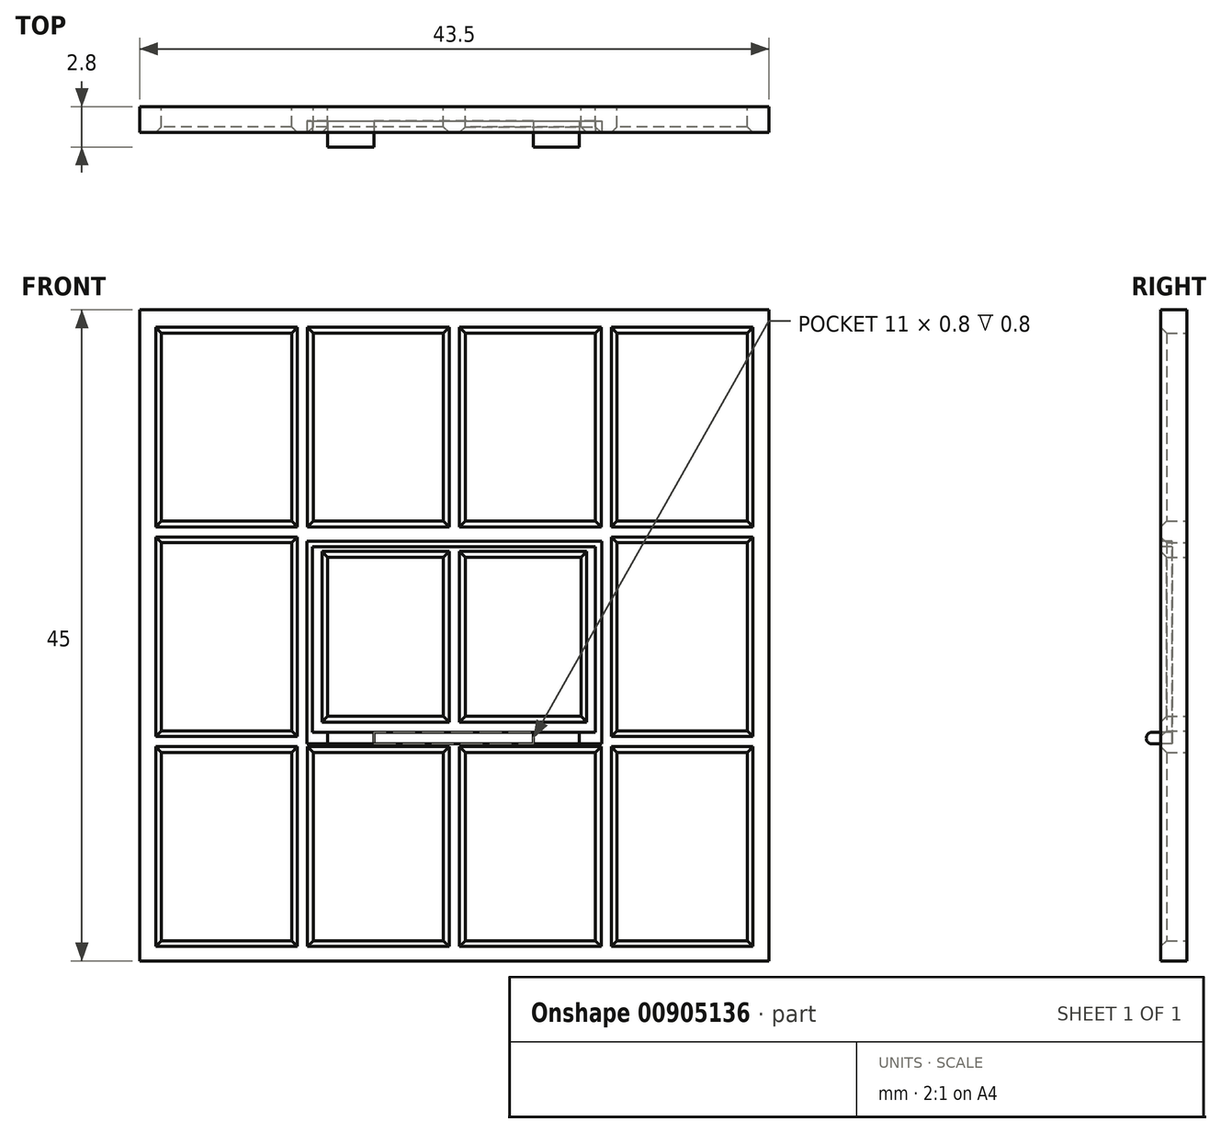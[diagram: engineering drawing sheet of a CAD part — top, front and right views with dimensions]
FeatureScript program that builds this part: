
annotation { "Feature Type Name" : "Feature", "Feature Type Description" : "" }
export const myFeature = defineFeature(function(context is Context, id is Id, definition is map)
    precondition{}
    {
        {
            var Q0;
            Q0=qCreatedBy(makeId("Front.planeOp"),FACE);
            var sketch = newSketch(context, id + "F0", { "sketchPlane" : qUnion([Q0])});
            skLineSegment(sketch, "E0.bottom", {"start": v(22, -22.5) * mm, "end": v(-22, -22.5) * mm});
            skLineSegment(sketch, "E0.top", {"start": v(22, 22.5) * mm, "end": v(-22, 22.5) * mm});
            skLineSegment(sketch, "E0.left", {"start": v(21.5, -22.5) * mm, "end": v(21.5, 22.5) * mm});
            skLineSegment(sketch, "E0.right", {"start": v(-22, -22.5) * mm, "end": v(-22, 22.5) * mm});
            skPoint(sketch, "E0.middle", {"position": v(-0.5, 0) * mm});
            skLineSegment(sketch, "E1", {"start": v(0, -22.5) * mm, "end": v(22, -22.5) * mm, "construction": true});
            skLineSegment(sketch, "E2", {"start": v(0, -22.5) * mm, "end": v(-22, -22.5) * mm, "construction": true});
            skLineSegment(sketch, "E3", {"start": v(-22, 22.5) * mm, "end": v(22, 22.5) * mm, "construction": true});
            skLineSegment(sketch, "E4", {"start": v(-22, 22.5) * mm, "end": v(-22, 7.5) * mm, "construction": true});
            skLineSegment(sketch, "E5", {"start": v(-22, 7.9) * mm, "end": v(22, 7.9) * mm, "construction": true});
            skLineSegment(sketch, "E6", {"start": v(-22, -22.5) * mm, "end": v(-22, -7.5) * mm});
            skLineSegment(sketch, "E7", {"start": v(-22, -7.1) * mm, "end": v(22, -7.1) * mm, "construction": true});
            skLineSegment(sketch, "E8", {"start": v(-22, -14.6) * mm, "end": v(-11, -14.6) * mm, "construction": true});
            skLineSegment(sketch, "E9", {"start": v(-16, -14.6) * mm, "end": v(-16, -7.1) * mm, "construction": true});
            skLineSegment(sketch, "E10.bottom", {"start": v(-20.5, -8.1) * mm, "end": v(-11.5, -8.1) * mm});
            skLineSegment(sketch, "E10.top", {"start": v(-20.5, -21.1) * mm, "end": v(-11.5, -21.1) * mm});
            skLineSegment(sketch, "E10.left", {"start": v(-20.5, -8.1) * mm, "end": v(-20.5, -21.1) * mm});
            skLineSegment(sketch, "E10.right", {"start": v(-11.5, -8.1) * mm, "end": v(-11.5, -21.1) * mm});
            skPoint(sketch, "E10.middle", {"position": v(-16, -14.6) * mm});
            skLineSegment(sketch, "E11.1.0.0", {"start": v(-10, -8.1) * mm, "end": v(-1, -8.1) * mm});
            skLineSegment(sketch, "E11.1.0.1", {"start": v(-1, -8.1) * mm, "end": v(-1, -21.1) * mm});
            skLineSegment(sketch, "E11.1.0.2", {"start": v(-10, -21.1) * mm, "end": v(-1, -21.1) * mm});
            skLineSegment(sketch, "E11.1.0.3", {"start": v(-10, -8.1) * mm, "end": v(-10, -21.1) * mm});
            skLineSegment(sketch, "E11.2.0.0", {"start": v(0.5, -8.1) * mm, "end": v(9.5, -8.1) * mm});
            skLineSegment(sketch, "E11.2.0.1", {"start": v(9.5, -8.1) * mm, "end": v(9.5, -21.1) * mm});
            skLineSegment(sketch, "E11.2.0.2", {"start": v(0.5, -21.1) * mm, "end": v(9.5, -21.1) * mm});
            skLineSegment(sketch, "E11.2.0.3", {"start": v(0.5, -8.1) * mm, "end": v(0.5, -21.1) * mm});
            skLineSegment(sketch, "E11.3.0.0", {"start": v(11, -8.1) * mm, "end": v(20, -8.1) * mm});
            skLineSegment(sketch, "E11.3.0.1", {"start": v(20, -8.1) * mm, "end": v(20, -21.1) * mm});
            skLineSegment(sketch, "E11.3.0.2", {"start": v(11, -21.1) * mm, "end": v(20, -21.1) * mm});
            skLineSegment(sketch, "E11.3.0.3", {"start": v(11, -8.1) * mm, "end": v(11, -21.1) * mm});
            skLineSegment(sketch, "E12.1.0.0", {"start": v(-20.5, 6.4) * mm, "end": v(-11.5, 6.4) * mm});
            skLineSegment(sketch, "E12.1.0.1", {"start": v(-11.5, 6.4) * mm, "end": v(-11.5, -6.6) * mm});
            skLineSegment(sketch, "E12.1.0.2", {"start": v(-20.5, -6.6) * mm, "end": v(-11.5, -6.6) * mm});
            skLineSegment(sketch, "E12.1.0.3", {"start": v(-20.5, 6.4) * mm, "end": v(-20.5, -6.6) * mm});
            skLineSegment(sketch, "E12.1.0.4", {"start": v(-10, 6.4) * mm, "end": v(-10, -6.6) * mm});
            skLineSegment(sketch, "E12.1.0.5", {"start": v(-10, 6.4) * mm, "end": v(-1, 6.4) * mm});
            skLineSegment(sketch, "E12.1.0.6", {"start": v(-1, 6.4) * mm, "end": v(-1, -6.6) * mm});
            skLineSegment(sketch, "E12.1.0.7", {"start": v(-10, -6.6) * mm, "end": v(-1, -6.6) * mm});
            skLineSegment(sketch, "E12.1.0.8", {"start": v(0.5, -6.6) * mm, "end": v(9.5, -6.6) * mm});
            skLineSegment(sketch, "E12.1.0.9", {"start": v(0.5, 6.4) * mm, "end": v(0.5, -6.6) * mm});
            skLineSegment(sketch, "E12.1.0.10", {"start": v(0.5, 6.4) * mm, "end": v(9.5, 6.4) * mm});
            skLineSegment(sketch, "E12.1.0.11", {"start": v(9.5, 6.4) * mm, "end": v(9.5, -6.6) * mm});
            skLineSegment(sketch, "E12.1.0.12", {"start": v(11, 6.4) * mm, "end": v(11, -6.6) * mm});
            skLineSegment(sketch, "E12.1.0.13", {"start": v(11, 6.4) * mm, "end": v(20, 6.4) * mm});
            skLineSegment(sketch, "E12.1.0.14", {"start": v(20, 6.4) * mm, "end": v(20, -6.6) * mm});
            skLineSegment(sketch, "E12.1.0.15", {"start": v(11, -6.6) * mm, "end": v(20, -6.6) * mm});
            skLineSegment(sketch, "E12.2.0.0", {"start": v(-20.5, 20.9) * mm, "end": v(-11.5, 20.9) * mm});
            skLineSegment(sketch, "E12.2.0.1", {"start": v(-11.5, 20.9) * mm, "end": v(-11.5, 7.9) * mm});
            skLineSegment(sketch, "E12.2.0.2", {"start": v(-20.5, 7.9) * mm, "end": v(-11.5, 7.9) * mm});
            skLineSegment(sketch, "E12.2.0.3", {"start": v(-20.5, 20.9) * mm, "end": v(-20.5, 7.9) * mm});
            skLineSegment(sketch, "E12.2.0.4", {"start": v(-10, 20.9) * mm, "end": v(-10, 7.9) * mm});
            skLineSegment(sketch, "E12.2.0.5", {"start": v(-10, 20.9) * mm, "end": v(-1, 20.9) * mm});
            skLineSegment(sketch, "E12.2.0.6", {"start": v(-1, 20.9) * mm, "end": v(-1, 7.9) * mm});
            skLineSegment(sketch, "E12.2.0.7", {"start": v(-10, 7.9) * mm, "end": v(-1, 7.9) * mm});
            skLineSegment(sketch, "E12.2.0.8", {"start": v(0.5, 7.9) * mm, "end": v(9.5, 7.9) * mm});
            skLineSegment(sketch, "E12.2.0.9", {"start": v(0.5, 20.9) * mm, "end": v(0.5, 7.9) * mm});
            skLineSegment(sketch, "E12.2.0.10", {"start": v(0.5, 20.9) * mm, "end": v(9.5, 20.9) * mm});
            skLineSegment(sketch, "E12.2.0.11", {"start": v(9.5, 20.9) * mm, "end": v(9.5, 7.9) * mm});
            skLineSegment(sketch, "E12.2.0.12", {"start": v(11, 20.9) * mm, "end": v(11, 7.9) * mm});
            skLineSegment(sketch, "E12.2.0.13", {"start": v(11, 20.9) * mm, "end": v(20, 20.9) * mm});
            skLineSegment(sketch, "E12.2.0.14", {"start": v(20, 20.9) * mm, "end": v(20, 7.9) * mm});
            skLineSegment(sketch, "E12.2.0.15", {"start": v(11, 7.9) * mm, "end": v(20, 7.9) * mm});
            skLineSegment(sketch, "E12.direction1", {"start": v(-20.5, -21.1) * mm, "end": v(-20.5, -6.2) * mm, "construction": true});
            skLineSegment(sketch, "E13", {"start": v(-22, -22.5) * mm, "end": v(-24, -22.5) * mm});
            skLineSegment(sketch, "E14", {"start": v(-24, -22.5) * mm, "end": v(-24, -24.5) * mm});
            skLineSegment(sketch, "E15", {"start": v(24, -24.5) * mm, "end": v(24, -22.5) * mm});
            skLineSegment(sketch, "E16", {"start": v(22, -22.5) * mm, "end": v(24, -22.5) * mm});
            skLineSegment(sketch, "E17", {"start": v(-12, -8.1) * mm, "end": v(-10.5, -8.1) * mm, "construction": true});
            skLineSegment(sketch, "E18", {"start": v(-1, -8.1) * mm, "end": v(1, -8.1) * mm, "construction": true});
            skLineSegment(sketch, "E19", {"start": v(-10, -6.2) * mm, "end": v(-10, -8.1) * mm, "construction": true});
            skLineSegment(sketch, "E20", {"start": v(11, 7.9) * mm, "end": v(11, 6.4) * mm, "construction": true});
            skLineSegment(sketch, "E21", {"start": v(11, 20.9) * mm, "end": v(9.5, 20.9) * mm, "construction": true});
            skSolve(sketch);
        }
        {
            var Q0;
            {var subQ4=sQuery(id+"F0.wireOp",EDGE,"E0.left");Q0=makeQuery(id+"F0.imprint","IMPRINT",FACE,{"disambiguationData":[TD([[makeQuery(id+"F0.imprint","IMPRINT",EDGE,{"derivedFrom":subQ4}),1.0]])]});}
            extrude(context, id + "F1", {"entities" : qUnion([Q0]), "depth" : 1.8 * mm, "offsetDistance" : 25 * mm});
        }
        {
            var Q0;
            Q0=makeQuery(id+"F1.opExtrude","SWEPT_FACE",FACE,{"disambiguationData":[OSD([sQuery(id+"F0.wireOp",EDGE,"E12.1.0.11")])]});
            extrude(context, id + "F2", {"entities" : qUnion([Q0]), "operationType" : NewBodyOperationType.ADD, "depth" : 1 * mm, "offsetDistance" : 25 * mm});
        }
        {
            var Q0;
            Q0=makeQuery(id+"F1.opExtrude","SWEPT_FACE",FACE,{"disambiguationData":[OSD([sQuery(id+"F0.wireOp",EDGE,"E12.1.0.4")])]});
            extrude(context, id + "F3", {"entities" : qUnion([Q0]), "operationType" : NewBodyOperationType.ADD, "depth" : 1 * mm, "offsetDistance" : 25 * mm});
        }
        {
            var Q0;
            Q0=makeQuery(id+"F1.opExtrude","SWEPT_FACE",FACE,{"disambiguationData":[OSD([sQuery(id+"F0.wireOp",EDGE,"E12.1.0.5")])]});
            var Q1;
            Q1=makeQuery(id+"F1.opExtrude","SWEPT_FACE",FACE,{"disambiguationData":[OSD([sQuery(id+"F0.wireOp",EDGE,"E12.1.0.10")])]});
            extrude(context, id + "F4", {"entities" : qUnion([Q0, Q1]), "operationType" : NewBodyOperationType.ADD, "depth" : 1 * mm, "offsetDistance" : 25 * mm});
        }
        {
            var Q0;
            Q0=makeQuery(id+"F1.opExtrude","SWEPT_FACE",FACE,{"disambiguationData":[OSD([sQuery(id+"F0.wireOp",EDGE,"E12.1.0.7")])]});
            var Q1;
            Q1=makeQuery(id+"F1.opExtrude","SWEPT_FACE",FACE,{"disambiguationData":[OSD([sQuery(id+"F0.wireOp",EDGE,"E12.1.0.8")])]});
            extrude(context, id + "F5", {"entities" : qUnion([Q0, Q1]), "operationType" : NewBodyOperationType.ADD, "depth" : 1 * mm, "offsetDistance" : 25 * mm});
        }
        {
            var Q0;
            {var subQ0=sQuery(id+"F0.wireOp",EDGE,"E12.1.0.7");var subQ1=sQuery(id+"F0.wireOp",EDGE,"E12.1.0.8");var subQ2=sQuery(id+"F0.wireOp",EDGE,"E12.1.0.5");var subQ3=sQuery(id+"F0.wireOp",EDGE,"E12.1.0.10");var subQ4=sQuery(id+"F0.wireOp",EDGE,"E12.1.0.4");var subQ5=sQuery(id+"F0.wireOp",EDGE,"E12.1.0.11");Q0=makeQuery(id+"F5.boolean.opBoolean","MERGE",FACE,{"derivedFrom":[makeQuery(id+"F4.boolean.opBoolean","MERGE",FACE,{"derivedFrom":[makeQuery(id+"F3.boolean.opBoolean","MERGE",FACE,{"derivedFrom":[makeQuery(id+"F2.boolean.opBoolean","MERGE",FACE,{"derivedFrom":[makeQuery(id+"F1.opExtrude","CAP_FACE",FACE,{"disambiguationData":[OSD([sQuery(id+"F0.wireOp",EDGE,"E0.bottom"),sQuery(id+"F0.wireOp",EDGE,"E0.top"),sQuery(id+"F0.wireOp",EDGE,"E0.left"),sQuery(id+"F0.wireOp",EDGE,"E0.right"),sQuery(id+"F0.wireOp",EDGE,"E10.bottom"),sQuery(id+"F0.wireOp",EDGE,"E10.top"),sQuery(id+"F0.wireOp",EDGE,"E10.left"),sQuery(id+"F0.wireOp",EDGE,"E10.right"),sQuery(id+"F0.wireOp",EDGE,"E11.1.0.0"),sQuery(id+"F0.wireOp",EDGE,"E11.1.0.1"),sQuery(id+"F0.wireOp",EDGE,"E11.1.0.2"),sQuery(id+"F0.wireOp",EDGE,"E11.1.0.3"),sQuery(id+"F0.wireOp",EDGE,"E11.2.0.0"),sQuery(id+"F0.wireOp",EDGE,"E11.2.0.1"),sQuery(id+"F0.wireOp",EDGE,"E11.2.0.2"),sQuery(id+"F0.wireOp",EDGE,"E11.2.0.3"),sQuery(id+"F0.wireOp",EDGE,"E11.3.0.0"),sQuery(id+"F0.wireOp",EDGE,"E11.3.0.1"),sQuery(id+"F0.wireOp",EDGE,"E11.3.0.2"),sQuery(id+"F0.wireOp",EDGE,"E11.3.0.3"),sQuery(id+"F0.wireOp",EDGE,"E12.1.0.0"),sQuery(id+"F0.wireOp",EDGE,"E12.1.0.1"),sQuery(id+"F0.wireOp",EDGE,"E12.1.0.2"),sQuery(id+"F0.wireOp",EDGE,"E12.1.0.3"),subQ4,subQ2,sQuery(id+"F0.wireOp",EDGE,"E12.1.0.6"),subQ0,subQ1,sQuery(id+"F0.wireOp",EDGE,"E12.1.0.9"),subQ3,subQ5,sQuery(id+"F0.wireOp",EDGE,"E12.1.0.12"),sQuery(id+"F0.wireOp",EDGE,"E12.1.0.13"),sQuery(id+"F0.wireOp",EDGE,"E12.1.0.14"),sQuery(id+"F0.wireOp",EDGE,"E12.1.0.15"),sQuery(id+"F0.wireOp",EDGE,"E12.2.0.0"),sQuery(id+"F0.wireOp",EDGE,"E12.2.0.1"),sQuery(id+"F0.wireOp",EDGE,"E12.2.0.2"),sQuery(id+"F0.wireOp",EDGE,"E12.2.0.3"),sQuery(id+"F0.wireOp",EDGE,"E12.2.0.4"),sQuery(id+"F0.wireOp",EDGE,"E12.2.0.5"),sQuery(id+"F0.wireOp",EDGE,"E12.2.0.6"),sQuery(id+"F0.wireOp",EDGE,"E12.2.0.7"),sQuery(id+"F0.wireOp",EDGE,"E12.2.0.8"),sQuery(id+"F0.wireOp",EDGE,"E12.2.0.9"),sQuery(id+"F0.wireOp",EDGE,"E12.2.0.10"),sQuery(id+"F0.wireOp",EDGE,"E12.2.0.11"),sQuery(id+"F0.wireOp",EDGE,"E12.2.0.12"),sQuery(id+"F0.wireOp",EDGE,"E12.2.0.13"),sQuery(id+"F0.wireOp",EDGE,"E12.2.0.14"),sQuery(id+"F0.wireOp",EDGE,"E12.2.0.15")])],"isStart":false}),makeQuery(id+"F2.opExtrude","SWEPT_FACE",FACE,{"disambiguationData":[OSD([subQ5]),TDD([makeQuery(id+"F1.opExtrude","CAP_EDGE",EDGE,{"disambiguationData":[OSD([subQ5])],"isStart":false})])]})]}),makeQuery(id+"F3.opExtrude","SWEPT_FACE",FACE,{"disambiguationData":[OSD([subQ4]),TDD([makeQuery(id+"F1.opExtrude","CAP_EDGE",EDGE,{"disambiguationData":[OSD([subQ4])],"isStart":false})])]})]}),makeQuery(id+"F4.opExtrude","SWEPT_FACE",FACE,{"disambiguationData":[OSD([subQ3]),TDD([makeQuery(id+"F1.opExtrude","CAP_EDGE",EDGE,{"disambiguationData":[OSD([subQ3])],"isStart":false})])]}),makeQuery(id+"F4.opExtrude","SWEPT_FACE",FACE,{"disambiguationData":[OSD([subQ2]),TDD([makeQuery(id+"F1.opExtrude","CAP_EDGE",EDGE,{"disambiguationData":[OSD([subQ2])],"isStart":false})])]})]}),makeQuery(id+"F5.opExtrude","SWEPT_FACE",FACE,{"disambiguationData":[OSD([subQ1]),TDD([makeQuery(id+"F1.opExtrude","CAP_EDGE",EDGE,{"disambiguationData":[OSD([subQ1])],"isStart":false})])]}),makeQuery(id+"F5.opExtrude","SWEPT_FACE",FACE,{"disambiguationData":[OSD([subQ0]),TDD([makeQuery(id+"F1.opExtrude","CAP_EDGE",EDGE,{"disambiguationData":[OSD([subQ0])],"isStart":false})])]})]});}
            var sketch = newSketch(context, id + "F6", { "sketchPlane" : qUnion([Q0])});
            skPoint(sketch, "E22.middle", {"position": v(-0.3, 0) * mm});
            skLineSegment(sketch, "E23.bottom", {"start": v(9.9, -6.7) * mm, "end": v(-10.5, -6.7) * mm});
            skLineSegment(sketch, "E24", {"start": v(-10.5, -6.7) * mm, "end": v(-9, -6.7) * mm, "construction": true});
            skLineSegment(sketch, "E25", {"start": v(-9, -6.7) * mm, "end": v(-9, -7.5) * mm, "construction": true});
            skLineSegment(sketch, "E26", {"start": v(-9, -6.7) * mm, "end": v(-9, -7.5) * mm});
            skLineSegment(sketch, "E27", {"start": v(-9, -7.5) * mm, "end": v(-5.8, -7.5) * mm});
            skLineSegment(sketch, "E28", {"start": v(-5.8, -6.7) * mm, "end": v(-5.8, -7.5) * mm});
            skLineSegment(sketch, "E29", {"start": v(9.9, -6.7) * mm, "end": v(8.4, -6.7) * mm});
            skLineSegment(sketch, "E30", {"start": v(8.4, -7.5) * mm, "end": v(8.4, -6.7) * mm});
            skLineSegment(sketch, "E31", {"start": v(8.4, -7.5) * mm, "end": v(5.2, -7.5) * mm});
            skLineSegment(sketch, "E32", {"start": v(5.2, -6.7) * mm, "end": v(5.2, -7.5) * mm});
            skLineSegment(sketch, "E33", {"start": v(-1, -5.6) * mm, "end": v(0.5, -5.6) * mm, "construction": true});
            skLineSegment(sketch, "E34", {"start": v(0.5, -5.6) * mm, "end": v(-0.25, -5.6) * mm, "construction": true});
            skLineSegment(sketch, "E35", {"start": v(-0.25, -7.5) * mm, "end": v(-0.25, -5.6) * mm, "construction": true});
            skLineSegment(sketch, "E36", {"start": v(-0.25, -7.5) * mm, "end": v(9.95, -7.5) * mm});
            skLineSegment(sketch, "E37", {"start": v(-0.25, -7.5) * mm, "end": v(-10.45, -7.5) * mm});
            skLineSegment(sketch, "E38.bottom", {"start": v(-10.45, -7.5) * mm, "end": v(9.95, -7.5) * mm});
            skLineSegment(sketch, "E38.top", {"start": v(-10.45, 6.52) * mm, "end": v(9.95, 6.52) * mm});
            skLineSegment(sketch, "E38.left", {"start": v(-10.45, -7.5) * mm, "end": v(-10.45, 6.52) * mm});
            skLineSegment(sketch, "E38.right", {"start": v(9.95, -7.5) * mm, "end": v(9.95, 6.52) * mm});
            skLineSegment(sketch, "E39", {"start": v(-10.45, 6.52) * mm, "end": v(-10.45, 6.12) * mm, "construction": true});
            skLineSegment(sketch, "E40", {"start": v(-10.45, 6.12) * mm, "end": v(-10.05, 6.12) * mm, "construction": true});
            skLineSegment(sketch, "E41", {"start": v(9.9, -6.7) * mm, "end": v(9.5, -6.7) * mm, "construction": true});
            skLineSegment(sketch, "E42", {"start": v(9.5, -6.7) * mm, "end": v(9.5, -7.5) * mm, "construction": true});
            skLineSegment(sketch, "E43.bottom", {"start": v(-10.05, 6.12) * mm, "end": v(9.5, 6.12) * mm});
            skLineSegment(sketch, "E43.top", {"start": v(-10.05, -6.7) * mm, "end": v(9.5, -6.7) * mm});
            skLineSegment(sketch, "E43.left", {"start": v(-10.05, 6.12) * mm, "end": v(-10.05, -6.7) * mm});
            skLineSegment(sketch, "E43.right", {"start": v(9.5, 6.12) * mm, "end": v(9.5, -6.7) * mm});
            skLineSegment(sketch, "E44.bottom", {"start": v(-9, -6.7) * mm, "end": v(-5.8, -6.7) * mm});
            skSolve(sketch);
        }
        {
            var Q0;
            Q0=makeQuery(id+"F6.imprint","IMPRINT",FACE,{"disambiguationData":[TD([[makeQuery(id+"F6.imprint","IMPRINT",EDGE,{"derivedFrom":sQuery(id+"F6.wireOp",EDGE,"E22.bottom")}),-1.0]])]});
            var Q1;
            {var subQ0=sQuery(id+"F6.wireOp",EDGE,"E28");Q1=makeQuery(id+"F6.imprint","IMPRINT",FACE,{"disambiguationData":[TD([[makeQuery(id+"F6.imprint","IMPRINT",EDGE,{"derivedFrom":subQ0}),1.0]])]});}
            var Q2;
            {var subQ7=sQuery(id+"F6.wireOp",EDGE,"E26");Q2=makeQuery(id+"F6.imprint","IMPRINT",FACE,{"disambiguationData":[TD([[makeQuery(id+"F6.imprint","IMPRINT",EDGE,{"derivedFrom":subQ7}),-1.0]])]});}
            var Q3;
            {var subQ1=sQuery(id+"F6.wireOp",EDGE,"E30");Q3=makeQuery(id+"F6.imprint","IMPRINT",FACE,{"disambiguationData":[TD([[makeQuery(id+"F6.imprint","IMPRINT",EDGE,{"derivedFrom":subQ1}),-1.0]])]});}
            var Q4;
            {var subQ0=sQuery(id+"F6.wireOp",EDGE,"E32");Q4=makeQuery(id+"F6.imprint","IMPRINT",FACE,{"disambiguationData":[TD([[makeQuery(id+"F6.imprint","IMPRINT",EDGE,{"derivedFrom":subQ0}),-1.0]])]});}
            var Q5;
            {var subQ3=sQuery(id+"F6.wireOp",EDGE,"E26");Q5=makeQuery(id+"F6.imprint","IMPRINT",FACE,{"disambiguationData":[TD([[makeQuery(id+"F6.imprint","IMPRINT",EDGE,{"derivedFrom":subQ3}),-1.0]])]});}
            extrude(context, id + "F7", {"entities" : qUnion([Q0, Q1, Q2, Q3, Q4, Q5]), "operationType" : NewBodyOperationType.REMOVE, "oppositeDirection" : true, "depth" : .8 * mm, "offsetDistance" : 25 * mm});
        }
        {
            var Q0;
            {var subQ0=sQuery(id+"F0.wireOp",EDGE,"E12.1.0.7");var subQ1=sQuery(id+"F0.wireOp",EDGE,"E12.1.0.8");var subQ2=sQuery(id+"F0.wireOp",EDGE,"E12.1.0.5");var subQ3=sQuery(id+"F0.wireOp",EDGE,"E12.1.0.10");var subQ4=sQuery(id+"F0.wireOp",EDGE,"E12.1.0.4");var subQ5=sQuery(id+"F0.wireOp",EDGE,"E12.1.0.11");Q0=makeQuery(id+"F5.boolean.opBoolean","MERGE",FACE,{"derivedFrom":[makeQuery(id+"F4.boolean.opBoolean","MERGE",FACE,{"derivedFrom":[makeQuery(id+"F3.boolean.opBoolean","MERGE",FACE,{"derivedFrom":[makeQuery(id+"F2.boolean.opBoolean","MERGE",FACE,{"derivedFrom":[makeQuery(id+"F1.opExtrude","CAP_FACE",FACE,{"disambiguationData":[OSD([sQuery(id+"F0.wireOp",EDGE,"E0.bottom"),sQuery(id+"F0.wireOp",EDGE,"E0.top"),sQuery(id+"F0.wireOp",EDGE,"E0.left"),sQuery(id+"F0.wireOp",EDGE,"E0.right"),sQuery(id+"F0.wireOp",EDGE,"E10.bottom"),sQuery(id+"F0.wireOp",EDGE,"E10.top"),sQuery(id+"F0.wireOp",EDGE,"E10.left"),sQuery(id+"F0.wireOp",EDGE,"E10.right"),sQuery(id+"F0.wireOp",EDGE,"E11.1.0.0"),sQuery(id+"F0.wireOp",EDGE,"E11.1.0.1"),sQuery(id+"F0.wireOp",EDGE,"E11.1.0.2"),sQuery(id+"F0.wireOp",EDGE,"E11.1.0.3"),sQuery(id+"F0.wireOp",EDGE,"E11.2.0.0"),sQuery(id+"F0.wireOp",EDGE,"E11.2.0.1"),sQuery(id+"F0.wireOp",EDGE,"E11.2.0.2"),sQuery(id+"F0.wireOp",EDGE,"E11.2.0.3"),sQuery(id+"F0.wireOp",EDGE,"E11.3.0.0"),sQuery(id+"F0.wireOp",EDGE,"E11.3.0.1"),sQuery(id+"F0.wireOp",EDGE,"E11.3.0.2"),sQuery(id+"F0.wireOp",EDGE,"E11.3.0.3"),sQuery(id+"F0.wireOp",EDGE,"E12.1.0.0"),sQuery(id+"F0.wireOp",EDGE,"E12.1.0.1"),sQuery(id+"F0.wireOp",EDGE,"E12.1.0.2"),sQuery(id+"F0.wireOp",EDGE,"E12.1.0.3"),subQ4,subQ2,sQuery(id+"F0.wireOp",EDGE,"E12.1.0.6"),subQ0,subQ1,sQuery(id+"F0.wireOp",EDGE,"E12.1.0.9"),subQ3,subQ5,sQuery(id+"F0.wireOp",EDGE,"E12.1.0.12"),sQuery(id+"F0.wireOp",EDGE,"E12.1.0.13"),sQuery(id+"F0.wireOp",EDGE,"E12.1.0.14"),sQuery(id+"F0.wireOp",EDGE,"E12.1.0.15"),sQuery(id+"F0.wireOp",EDGE,"E12.2.0.0"),sQuery(id+"F0.wireOp",EDGE,"E12.2.0.1"),sQuery(id+"F0.wireOp",EDGE,"E12.2.0.2"),sQuery(id+"F0.wireOp",EDGE,"E12.2.0.3"),sQuery(id+"F0.wireOp",EDGE,"E12.2.0.4"),sQuery(id+"F0.wireOp",EDGE,"E12.2.0.5"),sQuery(id+"F0.wireOp",EDGE,"E12.2.0.6"),sQuery(id+"F0.wireOp",EDGE,"E12.2.0.7"),sQuery(id+"F0.wireOp",EDGE,"E12.2.0.8"),sQuery(id+"F0.wireOp",EDGE,"E12.2.0.9"),sQuery(id+"F0.wireOp",EDGE,"E12.2.0.10"),sQuery(id+"F0.wireOp",EDGE,"E12.2.0.11"),sQuery(id+"F0.wireOp",EDGE,"E12.2.0.12"),sQuery(id+"F0.wireOp",EDGE,"E12.2.0.13"),sQuery(id+"F0.wireOp",EDGE,"E12.2.0.14"),sQuery(id+"F0.wireOp",EDGE,"E12.2.0.15")])],"isStart":false}),makeQuery(id+"F2.opExtrude","SWEPT_FACE",FACE,{"disambiguationData":[OSD([subQ5]),TDD([makeQuery(id+"F1.opExtrude","CAP_EDGE",EDGE,{"disambiguationData":[OSD([subQ5])],"isStart":false})])]})]}),makeQuery(id+"F3.opExtrude","SWEPT_FACE",FACE,{"disambiguationData":[OSD([subQ4]),TDD([makeQuery(id+"F1.opExtrude","CAP_EDGE",EDGE,{"disambiguationData":[OSD([subQ4])],"isStart":false})])]})]}),makeQuery(id+"F4.opExtrude","SWEPT_FACE",FACE,{"disambiguationData":[OSD([subQ3]),TDD([makeQuery(id+"F1.opExtrude","CAP_EDGE",EDGE,{"disambiguationData":[OSD([subQ3])],"isStart":false})])]}),makeQuery(id+"F4.opExtrude","SWEPT_FACE",FACE,{"disambiguationData":[OSD([subQ2]),TDD([makeQuery(id+"F1.opExtrude","CAP_EDGE",EDGE,{"disambiguationData":[OSD([subQ2])],"isStart":false})])]})]}),makeQuery(id+"F5.opExtrude","SWEPT_FACE",FACE,{"disambiguationData":[OSD([subQ1]),TDD([makeQuery(id+"F1.opExtrude","CAP_EDGE",EDGE,{"disambiguationData":[OSD([subQ1])],"isStart":false})])]}),makeQuery(id+"F5.opExtrude","SWEPT_FACE",FACE,{"disambiguationData":[OSD([subQ0]),TDD([makeQuery(id+"F1.opExtrude","CAP_EDGE",EDGE,{"disambiguationData":[OSD([subQ0])],"isStart":false})])]})]});}
            var sketch = newSketch(context, id + "F8", { "sketchPlane" : qUnion([Q0])});
            skLineSegment(sketch, "E45.left", {"start": v(-10.45, -7.5) * mm, "end": v(-10.45, -8.3) * mm});
            skLineSegment(sketch, "E46.bottom", {"start": v(5.2, -6.7) * mm, "end": v(8.4, -6.7) * mm});
            skLineSegment(sketch, "E46.top", {"start": v(5.2, -7.5) * mm, "end": v(8.4, -7.5) * mm});
            skLineSegment(sketch, "E46.left", {"start": v(5.2, -6.7) * mm, "end": v(5.2, -7.5) * mm});
            skLineSegment(sketch, "E46.right", {"start": v(8.4, -6.7) * mm, "end": v(8.4, -7.5) * mm});
            skLineSegment(sketch, "E47.bottom", {"start": v(-9, -6.7) * mm, "end": v(-5.8, -6.7) * mm});
            skLineSegment(sketch, "E47.top", {"start": v(-9, -7.5) * mm, "end": v(-5.8, -7.5) * mm});
            skLineSegment(sketch, "E47.left", {"start": v(-9, -6.7) * mm, "end": v(-9, -7.5) * mm});
            skLineSegment(sketch, "E47.right", {"start": v(-5.8, -6.7) * mm, "end": v(-5.8, -7.5) * mm});
            skSolve(sketch);
        }
        {
            var Q0;
            Q0=makeQuery(id+"F8.imprint","IMPRINT",FACE,{"disambiguationData":[TD([[makeQuery(id+"F8.imprint","IMPRINT",EDGE,{"derivedFrom":sQuery(id+"F8.wireOp",EDGE,"E46.bottom")}),-1.0]])]});
            var Q1;
            Q1=makeQuery(id+"F8.imprint","IMPRINT",FACE,{"disambiguationData":[TD([[makeQuery(id+"F8.imprint","IMPRINT",EDGE,{"derivedFrom":sQuery(id+"F8.wireOp",EDGE,"E45.bottom")}),1.0]])]});
            var Q2;
            Q2=makeQuery(id+"F8.imprint","IMPRINT",FACE,{"disambiguationData":[TD([[makeQuery(id+"F8.imprint","IMPRINT",EDGE,{"derivedFrom":sQuery(id+"F8.wireOp",EDGE,"E47.bottom")}),-1.0]])]});
            extrude(context, id + "F9", {"entities" : qUnion([Q0, Q1, Q2]), "operationType" : NewBodyOperationType.ADD, "depth" : 1 * mm, "offsetDistance" : 25 * mm});
        }
        {
            var Q0;
            Q0=makeQuery(id+"F9.opExtrude","CAP_EDGE",EDGE,{"disambiguationData":[OSD([sQuery(id+"F8.wireOp",EDGE,"E45.bottom")])],"isStart":false});
            var Q1;
            Q1=makeQuery(id+"F9.opExtrude","CAP_EDGE",EDGE,{"disambiguationData":[OSD([sQuery(id+"F8.wireOp",EDGE,"E45.top")])],"isStart":false});
            var Q2;
            Q2=makeQuery(id+"F9.opExtrude","CAP_EDGE",EDGE,{"disambiguationData":[OSD([sQuery(id+"F8.wireOp",EDGE,"E46.bottom")])],"isStart":false});
            var Q3;
            Q3=makeQuery(id+"F9.opExtrude","CAP_EDGE",EDGE,{"disambiguationData":[OSD([sQuery(id+"F8.wireOp",EDGE,"E46.top")])],"isStart":false});
            var Q4;
            Q4=makeQuery(id+"F9.opExtrude","CAP_EDGE",EDGE,{"disambiguationData":[OSD([sQuery(id+"F8.wireOp",EDGE,"E47.top")])],"isStart":false});
            var Q5;
            Q5=makeQuery(id+"F9.opExtrude","CAP_EDGE",EDGE,{"disambiguationData":[OSD([sQuery(id+"F8.wireOp",EDGE,"E47.bottom")])],"isStart":false});
            fillet(context, id + "F10", {"entities" : qUnion([Q0, Q1, Q2, Q3, Q4, Q5]), "radius" : .4 * mm, "tangentPropagation" : true, "allowEdgeOverflow" : false});
        }
        {
            var Q0;
            Q0=makeQuery(id+"F1.opExtrude","CAP_EDGE",EDGE,{"disambiguationData":[OSD([sQuery(id+"F0.wireOp",EDGE,"E12.2.0.3")])],"isStart":false});
            var Q1;
            Q1=makeQuery(id+"F1.opExtrude","CAP_EDGE",EDGE,{"disambiguationData":[OSD([sQuery(id+"F0.wireOp",EDGE,"E12.2.0.1")])],"isStart":false});
            var Q2;
            Q2=makeQuery(id+"F1.opExtrude","CAP_EDGE",EDGE,{"disambiguationData":[OSD([sQuery(id+"F0.wireOp",EDGE,"E12.2.0.0")])],"isStart":false});
            var Q3;
            Q3=makeQuery(id+"F1.opExtrude","CAP_EDGE",EDGE,{"disambiguationData":[OSD([sQuery(id+"F0.wireOp",EDGE,"E12.2.0.2")])],"isStart":false});
            var Q4;
            Q4=makeQuery(id+"F1.opExtrude","CAP_EDGE",EDGE,{"disambiguationData":[OSD([sQuery(id+"F0.wireOp",EDGE,"E12.1.0.0")])],"isStart":false});
            var Q5;
            Q5=makeQuery(id+"F1.opExtrude","CAP_EDGE",EDGE,{"disambiguationData":[OSD([sQuery(id+"F0.wireOp",EDGE,"E12.1.0.3")])],"isStart":false});
            var Q6;
            Q6=makeQuery(id+"F1.opExtrude","CAP_EDGE",EDGE,{"disambiguationData":[OSD([sQuery(id+"F0.wireOp",EDGE,"E12.1.0.2")])],"isStart":false});
            var Q7;
            Q7=makeQuery(id+"F1.opExtrude","CAP_EDGE",EDGE,{"disambiguationData":[OSD([sQuery(id+"F0.wireOp",EDGE,"E12.1.0.1")])],"isStart":false});
            var Q8;
            Q8=makeQuery(id+"F1.opExtrude","CAP_EDGE",EDGE,{"disambiguationData":[OSD([sQuery(id+"F0.wireOp",EDGE,"E12.2.0.7")])],"isStart":false});
            var Q9;
            Q9=makeQuery(id+"F1.opExtrude","CAP_EDGE",EDGE,{"disambiguationData":[OSD([sQuery(id+"F0.wireOp",EDGE,"E12.2.0.4")])],"isStart":false});
            var Q10;
            Q10=makeQuery(id+"F1.opExtrude","CAP_EDGE",EDGE,{"disambiguationData":[OSD([sQuery(id+"F0.wireOp",EDGE,"E12.2.0.6")])],"isStart":false});
            var Q11;
            Q11=makeQuery(id+"F1.opExtrude","CAP_EDGE",EDGE,{"disambiguationData":[OSD([sQuery(id+"F0.wireOp",EDGE,"E12.2.0.9")])],"isStart":false});
            var Q12;
            Q12=makeQuery(id+"F1.opExtrude","CAP_EDGE",EDGE,{"disambiguationData":[OSD([sQuery(id+"F0.wireOp",EDGE,"E12.2.0.8")])],"isStart":false});
            var Q13;
            Q13=makeQuery(id+"F1.opExtrude","CAP_EDGE",EDGE,{"disambiguationData":[OSD([sQuery(id+"F0.wireOp",EDGE,"E12.2.0.11")])],"isStart":false});
            var Q14;
            {var subQ0=sQuery(id+"F0.wireOp",EDGE,"E12.1.0.5");Q14=makeQuery(id+"F4.opExtrude","CAP_EDGE",EDGE,{"disambiguationData":[OSD([subQ0]),TDD([makeQuery(id+"F1.opExtrude","CAP_EDGE",EDGE,{"disambiguationData":[OSD([subQ0])],"isStart":false})])],"isStart":false});}
            var Q15;
            {var subQ0=sQuery(id+"F0.wireOp",EDGE,"E12.1.0.4");Q15=makeQuery(id+"F3.opExtrude","CAP_EDGE",EDGE,{"disambiguationData":[OSD([subQ0]),TDD([makeQuery(id+"F1.opExtrude","CAP_EDGE",EDGE,{"disambiguationData":[OSD([subQ0])],"isStart":false})])],"isStart":false});}
            var Q16;
            Q16=makeQuery(id+"F1.opExtrude","CAP_EDGE",EDGE,{"disambiguationData":[OSD([sQuery(id+"F0.wireOp",EDGE,"E12.1.0.6")])],"isStart":false});
            var Q17;
            Q17=makeQuery(id+"F1.opExtrude","CAP_EDGE",EDGE,{"disambiguationData":[OSD([sQuery(id+"F0.wireOp",EDGE,"E12.1.0.9")])],"isStart":false});
            var Q18;
            {var subQ0=sQuery(id+"F0.wireOp",EDGE,"E12.1.0.10");Q18=makeQuery(id+"F4.opExtrude","CAP_EDGE",EDGE,{"disambiguationData":[OSD([subQ0]),TDD([makeQuery(id+"F1.opExtrude","CAP_EDGE",EDGE,{"disambiguationData":[OSD([subQ0])],"isStart":false})])],"isStart":false});}
            var Q19;
            {var subQ0=sQuery(id+"F0.wireOp",EDGE,"E12.1.0.11");Q19=makeQuery(id+"F2.opExtrude","CAP_EDGE",EDGE,{"disambiguationData":[OSD([subQ0]),TDD([makeQuery(id+"F1.opExtrude","CAP_EDGE",EDGE,{"disambiguationData":[OSD([subQ0])],"isStart":false})])],"isStart":false});}
            var Q20;
            {var subQ0=sQuery(id+"F0.wireOp",EDGE,"E12.1.0.8");Q20=makeQuery(id+"F5.opExtrude","CAP_EDGE",EDGE,{"disambiguationData":[OSD([subQ0]),TDD([makeQuery(id+"F1.opExtrude","CAP_EDGE",EDGE,{"disambiguationData":[OSD([subQ0])],"isStart":false})])],"isStart":false});}
            var Q21;
            {var subQ0=sQuery(id+"F0.wireOp",EDGE,"E12.1.0.7");Q21=makeQuery(id+"F5.opExtrude","CAP_EDGE",EDGE,{"disambiguationData":[OSD([subQ0]),TDD([makeQuery(id+"F1.opExtrude","CAP_EDGE",EDGE,{"disambiguationData":[OSD([subQ0])],"isStart":false})])],"isStart":false});}
            var Q22;
            Q22=makeQuery(id+"F1.opExtrude","CAP_EDGE",EDGE,{"disambiguationData":[OSD([sQuery(id+"F0.wireOp",EDGE,"E12.2.0.5")])],"isStart":false});
            var Q23;
            Q23=makeQuery(id+"F1.opExtrude","CAP_EDGE",EDGE,{"disambiguationData":[OSD([sQuery(id+"F0.wireOp",EDGE,"E12.2.0.10")])],"isStart":false});
            var Q24;
            Q24=makeQuery(id+"F1.opExtrude","CAP_EDGE",EDGE,{"disambiguationData":[OSD([sQuery(id+"F0.wireOp",EDGE,"E12.2.0.13")])],"isStart":false});
            var Q25;
            Q25=makeQuery(id+"F1.opExtrude","CAP_EDGE",EDGE,{"disambiguationData":[OSD([sQuery(id+"F0.wireOp",EDGE,"E12.2.0.14")])],"isStart":false});
            var Q26;
            Q26=makeQuery(id+"F1.opExtrude","CAP_EDGE",EDGE,{"disambiguationData":[OSD([sQuery(id+"F0.wireOp",EDGE,"E12.2.0.15")])],"isStart":false});
            var Q27;
            Q27=makeQuery(id+"F1.opExtrude","CAP_EDGE",EDGE,{"disambiguationData":[OSD([sQuery(id+"F0.wireOp",EDGE,"E12.2.0.12")])],"isStart":false});
            var Q28;
            Q28=makeQuery(id+"F1.opExtrude","CAP_EDGE",EDGE,{"disambiguationData":[OSD([sQuery(id+"F0.wireOp",EDGE,"E12.1.0.13")])],"isStart":false});
            var Q29;
            Q29=makeQuery(id+"F1.opExtrude","CAP_EDGE",EDGE,{"disambiguationData":[OSD([sQuery(id+"F0.wireOp",EDGE,"E12.1.0.12")])],"isStart":false});
            var Q30;
            Q30=makeQuery(id+"F1.opExtrude","CAP_EDGE",EDGE,{"disambiguationData":[OSD([sQuery(id+"F0.wireOp",EDGE,"E12.1.0.14")])],"isStart":false});
            var Q31;
            Q31=makeQuery(id+"F1.opExtrude","CAP_EDGE",EDGE,{"disambiguationData":[OSD([sQuery(id+"F0.wireOp",EDGE,"E12.1.0.15")])],"isStart":false});
            var Q32;
            Q32=makeQuery(id+"F1.opExtrude","CAP_EDGE",EDGE,{"disambiguationData":[OSD([sQuery(id+"F0.wireOp",EDGE,"E11.3.0.0")])],"isStart":false});
            var Q33;
            Q33=makeQuery(id+"F1.opExtrude","CAP_EDGE",EDGE,{"disambiguationData":[OSD([sQuery(id+"F0.wireOp",EDGE,"E11.3.0.3")])],"isStart":false});
            var Q34;
            Q34=makeQuery(id+"F1.opExtrude","CAP_EDGE",EDGE,{"disambiguationData":[OSD([sQuery(id+"F0.wireOp",EDGE,"E11.3.0.2")])],"isStart":false});
            var Q35;
            Q35=makeQuery(id+"F1.opExtrude","CAP_EDGE",EDGE,{"disambiguationData":[OSD([sQuery(id+"F0.wireOp",EDGE,"E11.3.0.1")])],"isStart":false});
            var Q36;
            Q36=makeQuery(id+"F1.opExtrude","CAP_EDGE",EDGE,{"disambiguationData":[OSD([sQuery(id+"F0.wireOp",EDGE,"E11.2.0.1")])],"isStart":false});
            var Q37;
            Q37=makeQuery(id+"F1.opExtrude","CAP_EDGE",EDGE,{"disambiguationData":[OSD([sQuery(id+"F0.wireOp",EDGE,"E11.2.0.0")])],"isStart":false});
            var Q38;
            Q38=makeQuery(id+"F1.opExtrude","CAP_EDGE",EDGE,{"disambiguationData":[OSD([sQuery(id+"F0.wireOp",EDGE,"E11.2.0.3")])],"isStart":false});
            var Q39;
            Q39=makeQuery(id+"F1.opExtrude","CAP_EDGE",EDGE,{"disambiguationData":[OSD([sQuery(id+"F0.wireOp",EDGE,"E11.2.0.2")])],"isStart":false});
            var Q40;
            Q40=makeQuery(id+"F1.opExtrude","CAP_EDGE",EDGE,{"disambiguationData":[OSD([sQuery(id+"F0.wireOp",EDGE,"E11.1.0.2")])],"isStart":false});
            var Q41;
            Q41=makeQuery(id+"F1.opExtrude","CAP_EDGE",EDGE,{"disambiguationData":[OSD([sQuery(id+"F0.wireOp",EDGE,"E11.1.0.1")])],"isStart":false});
            var Q42;
            Q42=makeQuery(id+"F1.opExtrude","CAP_EDGE",EDGE,{"disambiguationData":[OSD([sQuery(id+"F0.wireOp",EDGE,"E11.1.0.0")])],"isStart":false});
            var Q43;
            Q43=makeQuery(id+"F1.opExtrude","CAP_EDGE",EDGE,{"disambiguationData":[OSD([sQuery(id+"F0.wireOp",EDGE,"E11.1.0.3")])],"isStart":false});
            var Q44;
            Q44=makeQuery(id+"F1.opExtrude","CAP_EDGE",EDGE,{"disambiguationData":[OSD([sQuery(id+"F0.wireOp",EDGE,"E10.right")])],"isStart":false});
            var Q45;
            Q45=makeQuery(id+"F1.opExtrude","CAP_EDGE",EDGE,{"disambiguationData":[OSD([sQuery(id+"F0.wireOp",EDGE,"E10.bottom")])],"isStart":false});
            var Q46;
            Q46=makeQuery(id+"F1.opExtrude","CAP_EDGE",EDGE,{"disambiguationData":[OSD([sQuery(id+"F0.wireOp",EDGE,"E10.left")])],"isStart":false});
            var Q47;
            Q47=makeQuery(id+"F1.opExtrude","CAP_EDGE",EDGE,{"disambiguationData":[OSD([sQuery(id+"F0.wireOp",EDGE,"E10.top")])],"isStart":false});
            chamfer(context, id + "F11", {"entities" : qUnion([Q0, Q1, Q2, Q3, Q4, Q5, Q6, Q7, Q8, Q9, Q10, Q11, Q12, Q13, Q14, Q15, Q16, Q17, Q18, Q19, Q20, Q21, Q22, Q23, Q24, Q25, Q26, Q27, Q28, Q29, Q30, Q31, Q32, Q33, Q34, Q35, Q36, Q37, Q38, Q39, Q40, Q41, Q42, Q43, Q44, Q45, Q46, Q47]), "width" : .4 * mm, "tangentPropagation" : true});
        }
    });
